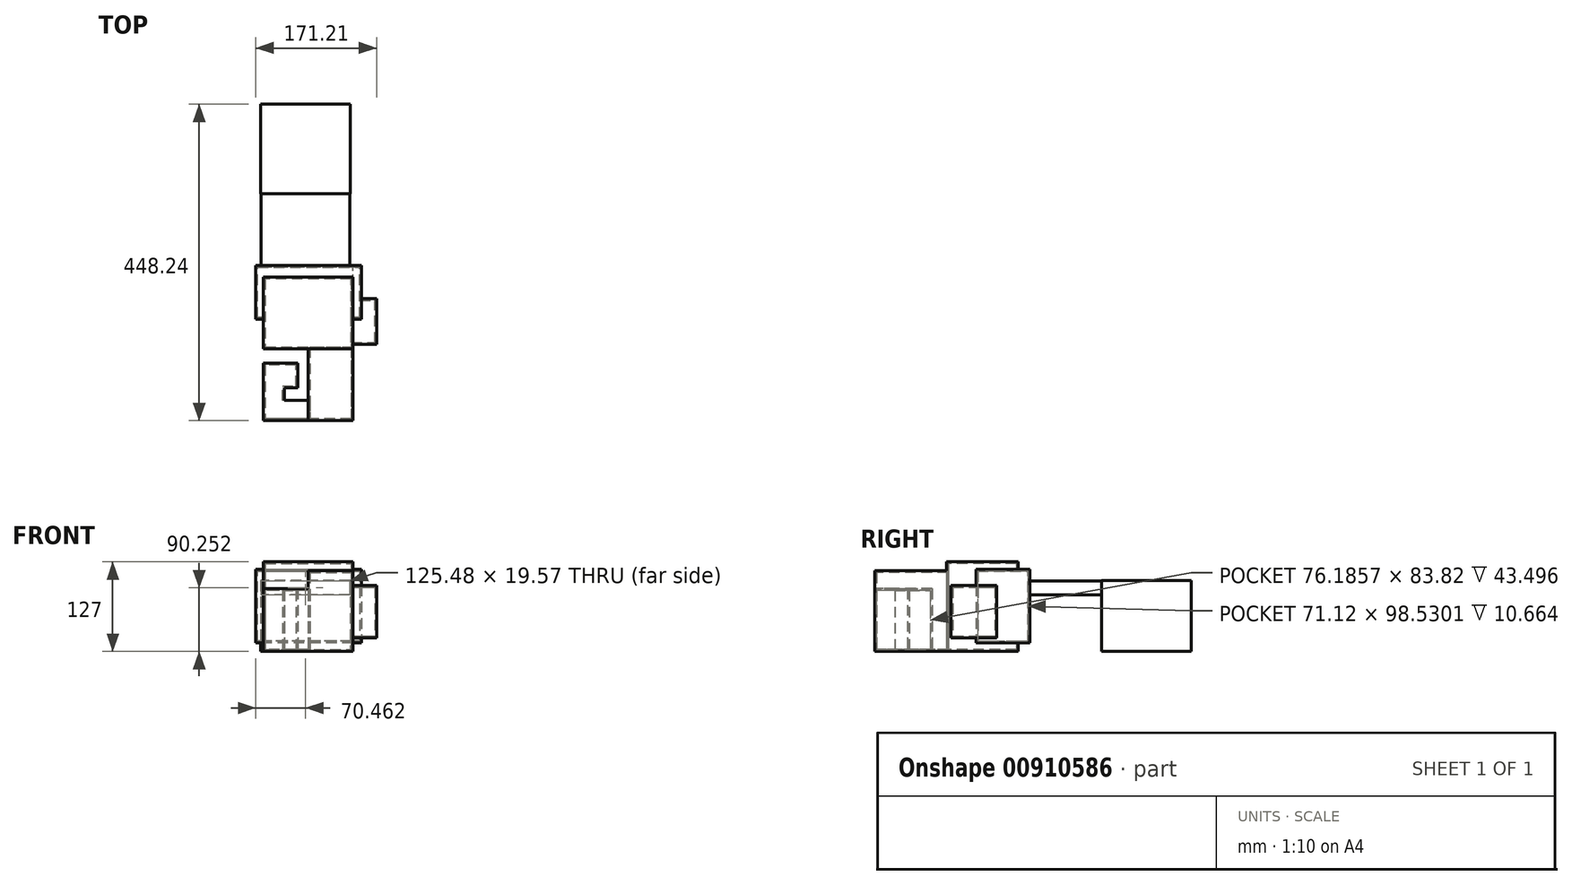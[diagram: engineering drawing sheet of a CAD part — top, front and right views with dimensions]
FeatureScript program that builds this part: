
annotation { "Feature Type Name" : "Feature", "Feature Type Description" : "" }
export const myFeature = defineFeature(function(context is Context, id is Id, definition is map)
    precondition{}
    {
        {
            var Q0;
            Q0=qCreatedBy(makeId("Top.planeOp"),FACE);
            var sketch = newSketch(context, id + "F0", { "sketchPlane" : qUnion([Q0])});
            skLineSegment(sketch, "E0.bottom", {"start": v(-99.33, 78.8) * mm, "end": v(27.67, 78.8) * mm});
            skLineSegment(sketch, "E0.top", {"start": v(-99.33, -22.8) * mm, "end": v(27.67, -22.8) * mm});
            skLineSegment(sketch, "E0.left", {"start": v(-99.33, 78.8) * mm, "end": v(-99.33, -22.8) * mm});
            skLineSegment(sketch, "E0.right", {"start": v(27.67, 78.8) * mm, "end": v(27.67, -22.8) * mm});
            skLineSegment(sketch, "E1.bottom", {"start": v(27.67, -22.8) * mm, "end": v(-35.83, -22.8) * mm});
            skLineSegment(sketch, "E1.top", {"start": v(27.67, -124.4) * mm, "end": v(-35.83, -124.4) * mm});
            skLineSegment(sketch, "E1.left", {"start": v(27.67, -22.8) * mm, "end": v(27.67, -124.4) * mm});
            skLineSegment(sketch, "E1.right", {"start": v(-35.83, -22.8) * mm, "end": v(-35.83, -124.4) * mm});
            skLineSegment(sketch, "E2", {"start": v(-35.83, -124.4) * mm, "end": v(-99.33, -124.4) * mm});
            skLineSegment(sketch, "E3", {"start": v(-35.83, -95.86) * mm, "end": v(-69.72, -95.86) * mm});
            skLineSegment(sketch, "E4", {"start": v(-69.72, -95.86) * mm, "end": v(-69.72, -85.94) * mm});
            skLineSegment(sketch, "E5", {"start": v(-69.72, -85.94) * mm, "end": v(-69.72, -78.06) * mm});
            skLineSegment(sketch, "E6", {"start": v(-69.72, -78.06) * mm, "end": v(-50.76, -78.06) * mm});
            skLineSegment(sketch, "E7", {"start": v(-50.76, -78.06) * mm, "end": v(-50.76, -43.13) * mm});
            skLineSegment(sketch, "E8", {"start": v(-50.76, -43.13) * mm, "end": v(-99.33, -43.13) * mm});
            skLineSegment(sketch, "E9", {"start": v(-99.33, -43.13) * mm, "end": v(-99.33, -124.4) * mm});
            skSolve(sketch);
        }
        {
            var Q0;
            Q0=makeQuery(id+"F0.imprint","IMPRINT",FACE,{"disambiguationData":[TD([[makeQuery(id+"F0.imprint","IMPRINT",EDGE,{"derivedFrom":sQuery(id+"F0.wireOp",EDGE,"E0.bottom")}),-1.0]])]});
            extrude(context, id + "F1", {"entities" : qUnion([Q0]), "depth" : 127 * mm, "offsetDistance" : 25.4 * mm});
        }
        {
            var Q0;
            {var subQ4=sQuery(id+"F0.wireOp",EDGE,"E1.top");Q0=makeQuery(id+"F0.imprint","IMPRINT",FACE,{"disambiguationData":[TD([[makeQuery(id+"F0.imprint","IMPRINT",EDGE,{"derivedFrom":subQ4}),-1.0]])]});}
            extrude(context, id + "F2", {"entities" : qUnion([Q0]), "operationType" : NewBodyOperationType.ADD, "depth" : 114.3 * mm, "offsetDistance" : 25.4 * mm});
        }
        {
            var Q0;
            {var subQ1=sQuery(id+"F0.wireOp",EDGE,"E2");Q0=makeQuery(id+"F0.imprint","IMPRINT",FACE,{"disambiguationData":[TD([[makeQuery(id+"F0.imprint","IMPRINT",EDGE,{"derivedFrom":subQ1}),-1.0]])]});}
            extrude(context, id + "F3", {"entities" : qUnion([Q0]), "operationType" : NewBodyOperationType.ADD, "depth" : 88.9 * mm, "offsetDistance" : 25.4 * mm});
        }
        {
            var Q0;
            Q0=qCreatedBy(makeId("Front.planeOp"),FACE);
            cPlane(context, id + "F4", {"entities" : qUnion([Q0]), "cplaneType" : CPlaneType.OFFSET, "offset" : 95.25 * mm, "oppositeDirection" : true, "width" : 152.4 * mm, "height" : 152.4 * mm});
        }
        {
            var Q0;
            Q0=qCreatedBy(id+"F4.planeOp",FACE);
            var sketch = newSketch(context, id + "F5", { "sketchPlane" : qUnion([Q0])});
            skLineSegment(sketch, "E10", {"start": v(27.77, 12.54) * mm, "end": v(-110, 12.54) * mm});
            skLineSegment(sketch, "E11", {"start": v(-110, 12.54) * mm, "end": v(-110, 116.15) * mm});
            skLineSegment(sketch, "E12", {"start": v(-110, 116.15) * mm, "end": v(39.66, 116.15) * mm});
            skLineSegment(sketch, "E13", {"start": v(39.66, 116.15) * mm, "end": v(39.66, 12.16) * mm});
            skLineSegment(sketch, "E14", {"start": v(39.66, 12.16) * mm, "end": v(27.77, 12.54) * mm});
            skSolve(sketch);
        }
        {
            var Q0;
            Q0=makeQuery(id+"F5.imprint","IMPRINT",FACE,{"disambiguationData":[TD([[makeQuery(id+"F5.imprint","IMPRINT",EDGE,{"derivedFrom":sQuery(id+"F5.wireOp",EDGE,"E10")}),-1.0]])]});
            extrude(context, id + "F6", {"entities" : qUnion([Q0]), "operationType" : NewBodyOperationType.ADD, "depth" : 76.2 * mm, "offsetDistance" : 25.4 * mm});
        }
        {
            var Q0;
            Q0=qCreatedBy(makeId("Right.planeOp"),FACE);
            cPlane(context, id + "F7", {"entities" : qUnion([Q0]), "cplaneType" : CPlaneType.OFFSET, "offset" : 61.2 * mm, "width" : 152.4 * mm, "height" : 152.4 * mm});
        }
        {
            var Q0;
            Q0=qCreatedBy(id+"F7.planeOp",FACE);
            var sketch = newSketch(context, id + "F8", { "sketchPlane" : qUnion([Q0])});
            skLineSegment(sketch, "E15.bottom", {"start": v(-16.3, 93.51) * mm, "end": v(48.55, 93.51) * mm});
            skLineSegment(sketch, "E15.top", {"start": v(-16.3, 19.45) * mm, "end": v(48.55, 19.45) * mm});
            skLineSegment(sketch, "E15.left", {"start": v(-16.3, 93.51) * mm, "end": v(-16.3, 19.45) * mm});
            skLineSegment(sketch, "E15.right", {"start": v(48.55, 93.51) * mm, "end": v(48.55, 19.45) * mm});
            skSolve(sketch);
        }
        {
            var Q0;
            Q0 = qSketchRegion(id + "F8", true);
            extrude(context, id + "F9", {"entities" : qUnion([Q0]), "operationType" : NewBodyOperationType.ADD, "oppositeDirection" : true, "depth" : 38.1 * mm, "offsetDistance" : 25.4 * mm});
        }
        {
            var Q0;
            Q0=makeQuery(id+"F3.opExtrude","SWEPT_FACE",FACE,{"disambiguationData":[OSD([sQuery(id+"F0.wireOp",EDGE,"E3")])]});
            shell(context, id + "F10", {"entities" : qUnion([Q0]), "thickness" : 2.54 * mm});
        }
        {
            var Q0;
            Q0=qCreatedBy(id+"F4.planeOp",FACE);
            var sketch = newSketch(context, id + "F11", { "sketchPlane" : qUnion([Q0])});
            skLineSegment(sketch, "E16.bottom", {"start": v(23.2, 100.04) * mm, "end": v(-102.28, 100.04) * mm});
            skLineSegment(sketch, "E16.top", {"start": v(23.2, 80.47) * mm, "end": v(-102.28, 80.47) * mm});
            skLineSegment(sketch, "E16.left", {"start": v(23.2, 100.04) * mm, "end": v(23.2, 80.47) * mm});
            skLineSegment(sketch, "E16.right", {"start": v(-102.28, 100.04) * mm, "end": v(-102.28, 80.47) * mm});
            skSolve(sketch);
        }
        {
            var Q0;
            Q0 = qSketchRegion(id + "F11", true);
            extrude(context, id + "F12", {"entities" : qUnion([Q0]), "operationType" : NewBodyOperationType.ADD, "oppositeDirection" : true, "depth" : 101.6 * mm, "offsetDistance" : 25.4 * mm});
        }
        {
            var Q0;
            Q0=qCreatedBy(id+"F4.planeOp",FACE);
            cPlane(context, id + "F13", {"entities" : qUnion([Q0]), "cplaneType" : CPlaneType.OFFSET, "offset" : 101.6 * mm, "oppositeDirection" : true, "width" : 152.4 * mm, "height" : 152.4 * mm});
        }
        {
            var Q0;
            Q0=qCreatedBy(id+"F13.planeOp",FACE);
            var sketch = newSketch(context, id + "F14", { "sketchPlane" : qUnion([Q0])});
            skLineSegment(sketch, "E17.bottom", {"start": v(23.87, 100.47) * mm, "end": v(-103.13, 100.47) * mm});
            skLineSegment(sketch, "E17.top", {"start": v(23.87, 0) * mm, "end": v(-103.13, 0) * mm});
            skLineSegment(sketch, "E17.left", {"start": v(23.87, 100.47) * mm, "end": v(23.87, 0) * mm});
            skLineSegment(sketch, "E17.right", {"start": v(-103.13, 100.47) * mm, "end": v(-103.13, 0) * mm});
            skSolve(sketch);
        }
        {
            var Q0;
            Q0 = qSketchRegion(id + "F14", true);
            extrude(context, id + "F15", {"entities" : qUnion([Q0]), "operationType" : NewBodyOperationType.ADD, "oppositeDirection" : true, "depth" : 127 * mm, "offsetDistance" : 25.4 * mm});
        }
        {
            var Q0;
            Q0=sQuery(id+"F14.wireOp",EDGE,"E17.right");
            var Q1;
            Q1=sQuery(id+"F14.wireOp",VERTEX,"E17.bottom.end");
            cPlane(context, id + "F16", {"entities" : qUnion([Q0, Q1]), "cplaneType" : CPlaneType.CURVE_POINT, "offset" : 25.4 * mm, "width" : 152.4 * mm, "height" : 152.4 * mm});
        }
    });
